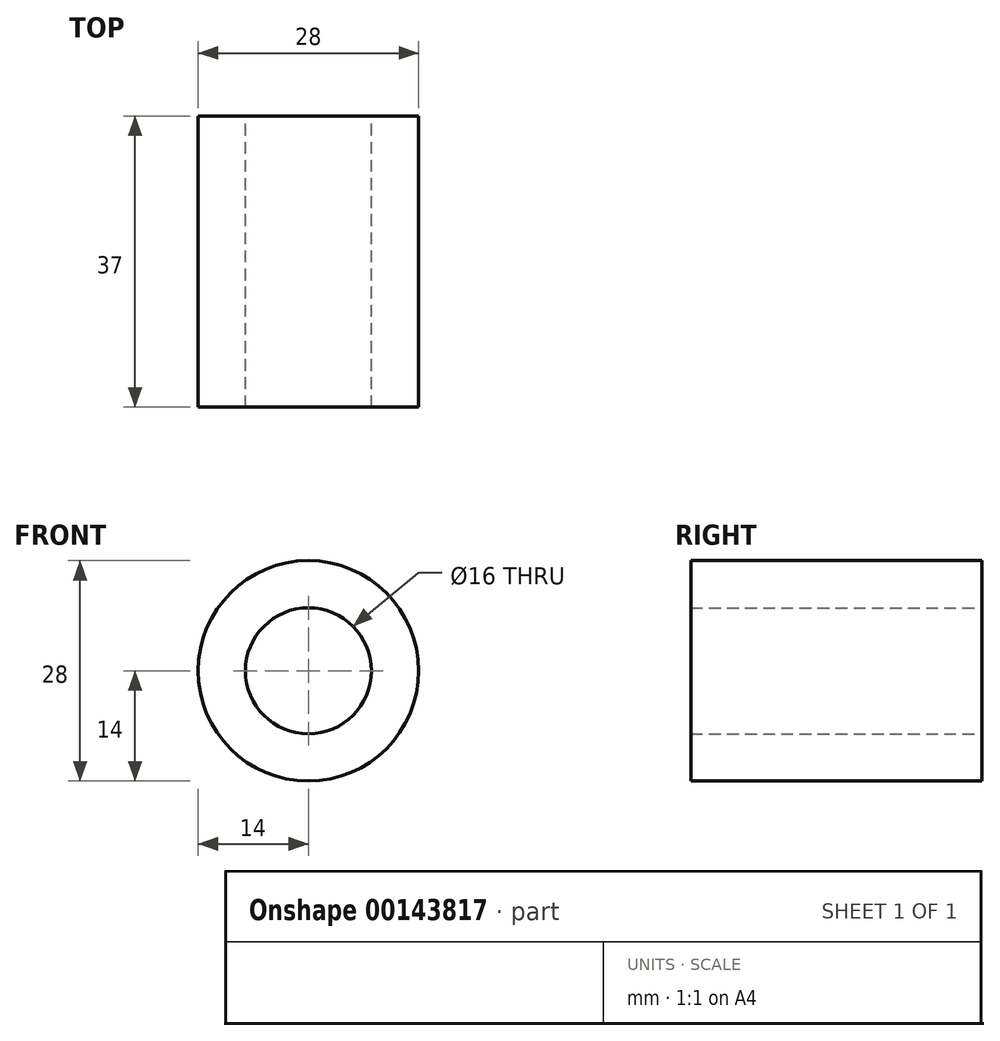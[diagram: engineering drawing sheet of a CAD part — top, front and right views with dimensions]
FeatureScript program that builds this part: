
annotation { "Feature Type Name" : "Feature", "Feature Type Description" : "" }
export const myFeature = defineFeature(function(context is Context, id is Id, definition is map)
    precondition{}
    {
        {
            var Q0;
            Q0=qCreatedBy(makeId("Front.planeOp"),FACE);
            var sketch = newSketch(context, id + "F0", { "sketchPlane" : qUnion([Q0])});
            skCircle(sketch, "E0", {"center": v(0, 0) * mm, "radius": 14 * mm});
            skCircle(sketch, "E1", {"center": v(0, 0) * mm, "radius": 8 * mm});
            skSolve(sketch);
        }
        {
            var Q0;
            Q0=makeQuery(id+"F0.imprint","IMPRINT",FACE,{"disambiguationData":[TD([[makeQuery(id+"F0.imprint","IMPRINT",EDGE,{"derivedFrom":sQuery(id+"F0.wireOp",EDGE,"E0")}),1.0]])]});
            extrude(context, id + "F1", {"entities" : qUnion([Q0]), "depth" : 37 * mm});
        }
    });
